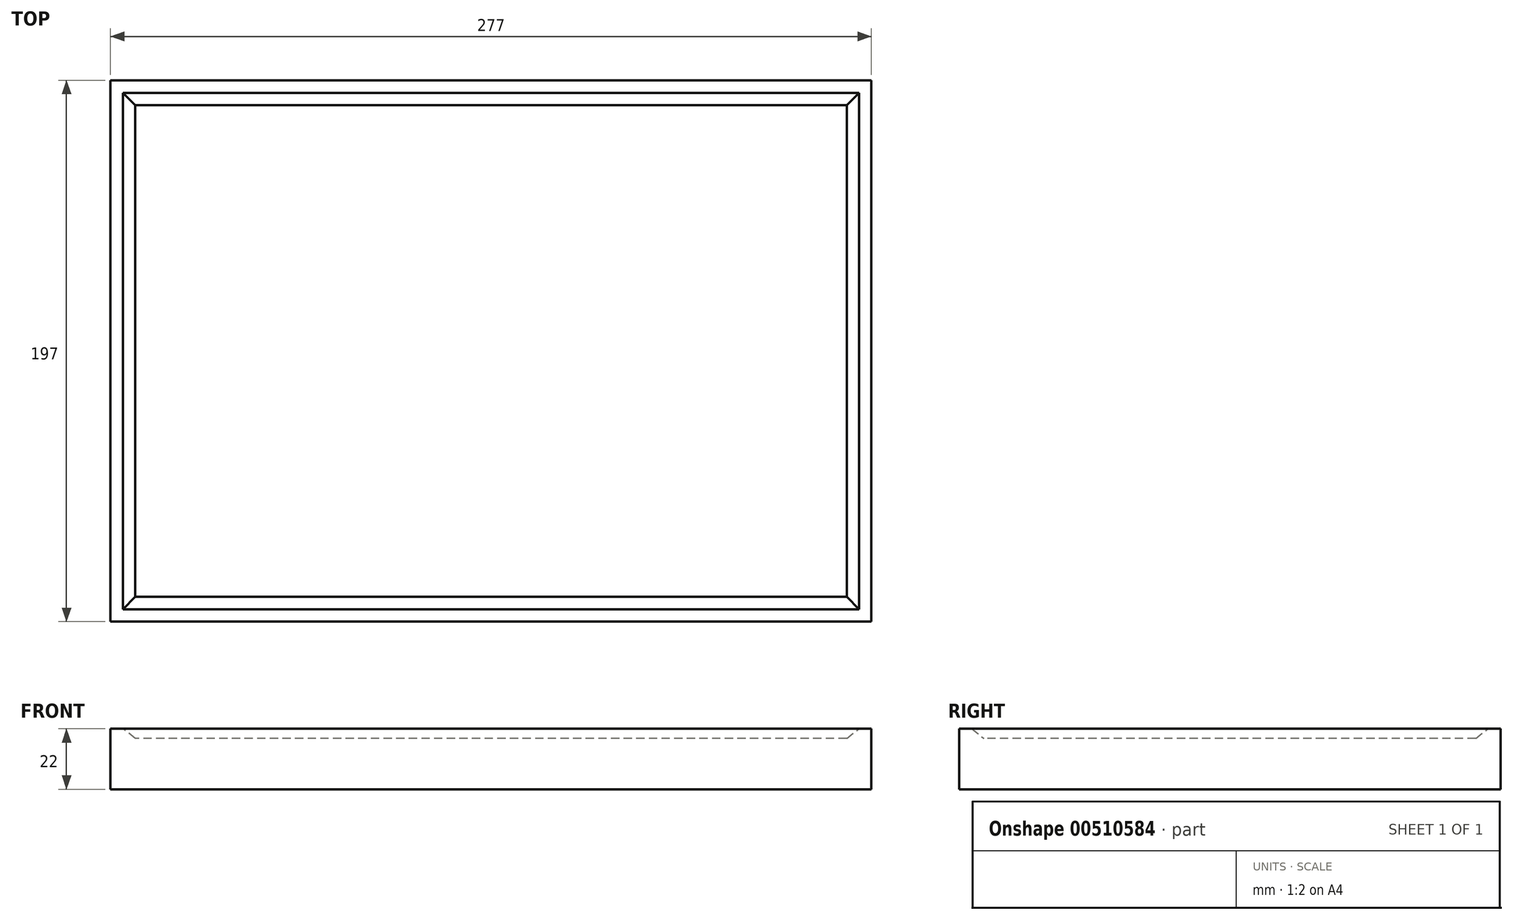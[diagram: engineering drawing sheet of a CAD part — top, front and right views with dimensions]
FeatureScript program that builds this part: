
annotation { "Feature Type Name" : "Feature", "Feature Type Description" : "" }
export const myFeature = defineFeature(function(context is Context, id is Id, definition is map)
    precondition{}
    {
        {
            var Q0;
            Q0=qCreatedBy(makeId("Top.planeOp"),FACE);
            var sketch = newSketch(context, id + "F0", { "sketchPlane" : qUnion([Q0])});
            skLineSegment(sketch, "E0.rect.bottom", {"start": v(138.5, -98.5) * mm, "end": v(-138.5, -98.5) * mm});
            skLineSegment(sketch, "E0.rect.top", {"start": v(138.5, 98.5) * mm, "end": v(-138.5, 98.5) * mm});
            skLineSegment(sketch, "E0.rect.left", {"start": v(138.5, -98.5) * mm, "end": v(138.5, 98.5) * mm});
            skLineSegment(sketch, "E0.rect.right", {"start": v(-138.5, -98.5) * mm, "end": v(-138.5, 98.5) * mm});
            skPoint(sketch, "E0.rect.middle", {"position": v(0, 0) * mm});
            skSolve(sketch);
        }
        {
            var Q0;
            Q0=qSketchRegion(id+"F0",true);
            var Q1;
            Q1=makeQuery(id+"F0.imprint","IMPRINT",FACE,{"disambiguationData":[TD([[makeQuery(id+"F0.imprint","IMPRINT",EDGE,{"derivedFrom":sQuery(id+"F0.wireOp",EDGE,"E0.rect.bottom")}),-1.0]])]});
            extrude(context, id + "F1", {"entities" : qUnion([Q0, Q1]), "depth" : 22 * mm});
        }
        {
            var Q0;
            Q0=makeQuery(id+"F1.opExtrude","CAP_FACE",FACE,{"disambiguationData":[OSD([sQuery(id+"F0.wireOp",EDGE,"E0.rect.bottom"),sQuery(id+"F0.wireOp",EDGE,"E0.rect.top"),sQuery(id+"F0.wireOp",EDGE,"E0.rect.left"),sQuery(id+"F0.wireOp",EDGE,"E0.rect.right")])],"isStart":false});
            var sketch = newSketch(context, id + "F2", { "sketchPlane" : qUnion([Q0])});
            skLineSegment(sketch, "E1.0", {"start": v(134, 94) * mm, "end": v(-134, 94) * mm});
            skLineSegment(sketch, "E1.1", {"start": v(134, -94) * mm, "end": v(134, 94) * mm});
            skLineSegment(sketch, "E1.2", {"start": v(134, -94) * mm, "end": v(-134, -94) * mm});
            skLineSegment(sketch, "E1.3", {"start": v(-134, -94) * mm, "end": v(-134, 94) * mm});
            skSolve(sketch);
        }
        {
            var Q0;
            Q0=qSketchRegion(id+"F2",true);
            extrude(context, id + "F3", {"entities" : qUnion([Q0]), "operationType" : NewBodyOperationType.REMOVE, "oppositeDirection" : true, "depth" : 3.5 * mm});
        }
        {
            var Q0;
            Q0=makeQuery(id+"F3.boolean.opBoolean","COPY",FACE,{"derivedFrom":makeQuery(id+"F3.opExtrude","CAP_FACE",FACE,{"disambiguationData":[OSD([sQuery(id+"F2.wireOp",EDGE,"E1.0"),sQuery(id+"F2.wireOp",EDGE,"E1.1"),sQuery(id+"F2.wireOp",EDGE,"E1.2"),sQuery(id+"F2.wireOp",EDGE,"E1.3")])],"isStart":false})});
            chamfer(context, id + "F4", {"entities" : qUnion([Q0]), "chamferType" : ChamferType.OFFSET_ANGLE, "width" : 4.5 * mm, "oppositeDirection" : false, "angle" : 38 * degree, "tangentPropagation" : true});
        }
    });
